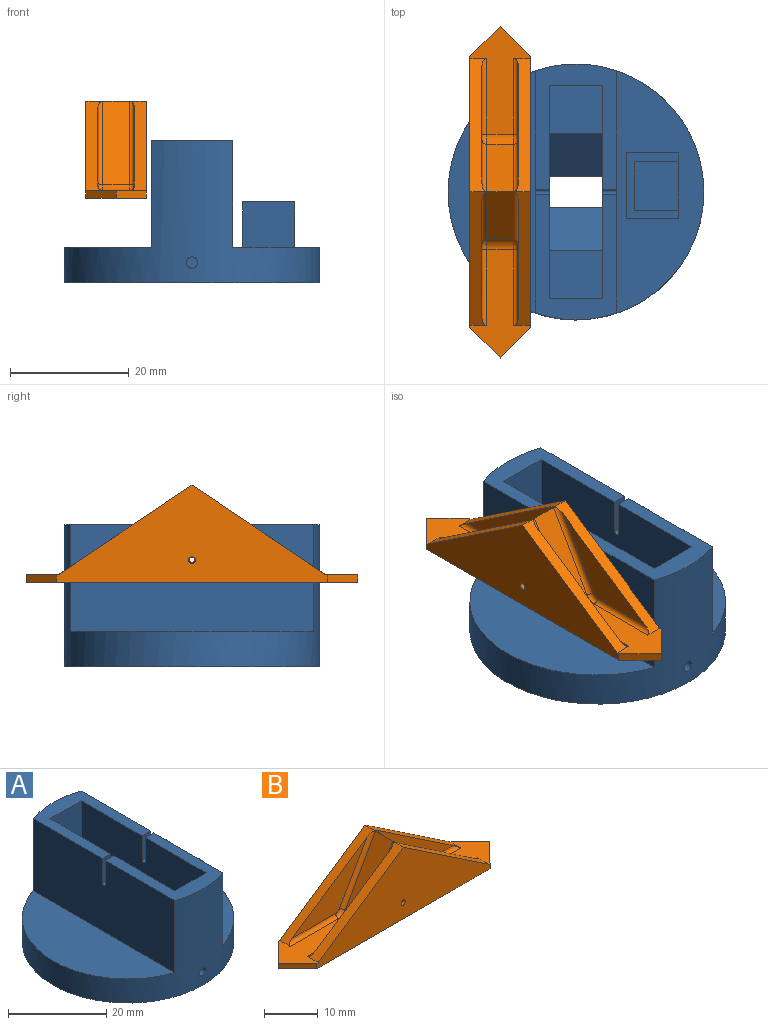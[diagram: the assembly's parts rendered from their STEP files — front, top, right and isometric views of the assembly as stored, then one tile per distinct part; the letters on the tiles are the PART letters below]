
ASSEMBLY  parts=2 mates=1
PART A: 39 faces, bbox 43.1x43.1x24 mm
  f0: cylinder r=21.57mm len=43.14mm, axis (0,0,-1), area 1313.1mm2, adj f3,f5,f6,f7,f9,f10,f14,f35
  f1: plane 7.48x0.75mm, normal (0,1,0), area 5.6mm2, adj f24,f27,f28,f32
  f2: plane 7.48x0.75mm, normal (0,-1,0), area 5.6mm2, adj f24,f27,f28,f32
  f3: plane 40.87x14.67mm, normal (0,0,1), area 340.8mm2, adj f0,f6,f24,f29,f31,f34
  f4: plane 9x8.08mm, normal (0,0,1), area 72.7mm2, adj f8,f12,f13,f21
  f5: plane 21.12x13.8mm, normal (0,0,1), area 128.3mm2, adj f0,f6,f7,f8,f11,f12,f16,f18
  f6: plane 40.87x18mm, normal (1,0,0), area 730mm2, adj f0,f3,f5,f14,f16,f17,f22
  f7: plane 40.87x18mm, normal (-1,0,0), area 730mm2, adj f0,f5,f9,f14,f18,f19,f23
  f8: plane 36x24mm, normal (1,0,0), area 717.5mm2, adj f4,f5,f10,f11,f13,f14,f15,f18
  f9: plane 40.87x14.67mm, normal (0,0,1), area 438.3mm2, adj f0,f7
  f10: plane 43.14x43.14mm, normal (0,0,-1), area 1414.7mm2, adj f0,f8,f12,f20,f21
  f11: plane 18x9mm, normal (0,-1,0), area 162mm2, adj f5,f8,f12,f15
  f12: plane 36x24mm, normal (-1,0,0), area 717.5mm2, adj f4,f5,f10,f11,f13,f14,f15,f16
  f13: plane 18x9mm, normal (0,1,0), area 162mm2, adj f4,f8,f12,f14
  f14: plane 21.12x13.8mm, normal (0,0,1), area 128.3mm2, adj f0,f6,f7,f8,f12,f13,f17,f19
  f15: plane 9x8.08mm, normal (0,0,1), area 72.7mm2, adj f8,f11,f12,f20
  f16: plane 6x2.4mm, normal (0,-1,0), area 14.4mm2, adj f5,f6,f12,f22
  f17: plane 6x2.4mm, normal (0,1,0), area 14.4mm2, adj f6,f12,f14,f22
  f18: plane 6x2.4mm, normal (0,-1,0), area 14.4mm2, adj f5,f7,f8,f23
  f19: plane 6x2.4mm, normal (0,1,0), area 14.4mm2, adj f7,f8,f14,f23
  f20: plane 9x7.32mm, normal (0,-0.63,0.77), area 85.2mm2, adj f8,f10,f12,f15
  f21: plane 9x7.32mm, normal (0,0.63,0.77), area 85.2mm2, adj f4,f8,f10,f12
  f22: cylinder r=0.45mm len=2.4mm, axis (-1,0,0), area 3.4mm2, adj f6,f12,f16,f17
  f23: cylinder r=0.45mm len=2.4mm, axis (-1,0,0), area 3.4mm2, adj f7,f8,f18,f19
  f24: plane 11.1x7.65mm, normal (1,0,0), area 70.1mm2, adj f1,f2,f3,f25,f26,f27,f28,f29
  f25: plane 9.6x8.04mm, normal (0,0,1), area 77.2mm2, adj f24,f26,f30,f33
  f26: plane 8.04x0.9mm, normal (0,1,0), area 7.2mm2, adj f24,f25,f27,f33
  f27: plane 9.6x8.04mm, normal (0,0,-1), area 15.5mm2, adj f1,f2,f24,f26,f30,f32,f33
  f28: plane 11.1x8.79mm, normal (0,0,1), area 35.8mm2, adj f1,f2,f24,f29,f31,f32,f34
  f29: plane 8.79x7.65mm, normal (0,-1,0), area 67.2mm2, adj f3,f24,f28,f34
  f30: plane 8.04x0.9mm, normal (0,-1,0), area 7.2mm2, adj f24,f25,f27,f33
  f31: plane 8.79x7.65mm, normal (0,1,0), area 67.2mm2, adj f3,f24,f28,f34
  f32: plane 8.25x0.75mm, normal (1,0,0), area 6.2mm2, adj f1,f2,f27,f28
  f33: plane 9.6x0.9mm, normal (1,0,0), area 8.6mm2, adj f25,f26,f27,f30
  f34: plane 11.1x7.65mm, normal (-1,0,0), area 84.9mm2, adj f3,f28,f29,f31
  f35: cylinder r=0.96mm len=7.5mm, axis (0,-1,0), area 45.2mm2, adj f0,f36
  f36: plane 1.92x1.92mm, normal (0,-1,0), area 2.9mm2, adj f35
  f37: cylinder r=0.96mm len=7.5mm, axis (0,1,0), area 45.2mm2, adj f0,f38
  f38: plane 1.92x1.92mm, normal (0,1,0), area 2.9mm2, adj f37
PART B: 34 faces, bbox 56x10.2x16.8 mm
  f0: plane 18.24x10.2mm, normal (0,0,1), area 87.7mm2, adj f3,f4,f8,f9,f13,f14,f19,f27
  f1: plane 19.82x13.32mm, normal (0,1,0), area 81.5mm2, adj f5,f24,f25,f26
  f2: plane 19.82x13.32mm, normal (0,-1,0), area 81.5mm2, adj f6,f21,f22,f23
  f3: plane 22.5x15.12mm, normal (0.56,0,0.83), area 55.9mm2, adj f0,f5,f8,f15,f30,f32
  f4: plane 22.5x15.12mm, normal (0.56,0,0.83), area 55.9mm2, adj f0,f6,f9,f16,f27,f29
  f5: plane 22.5x15.12mm, normal (-0.56,0,0.83), area 55.9mm2, adj f1,f3,f7,f8,f24,f26
  f6: plane 22.5x15.12mm, normal (-0.56,0,0.83), area 55.9mm2, adj f2,f4,f7,f9,f21,f23
  f7: plane 18.24x10.2mm, normal (0,0,1), area 87.7mm2, adj f5,f6,f8,f9,f11,f12,f20,f21
  f8: plane 45.84x16.4mm, normal (0,-1,0), area 397.9mm2, adj f0,f3,f5,f7,f10,f12,f14,f33
  f9: plane 45.83x16.4mm, normal (0,1,0), area 397.9mm2, adj f0,f4,f6,f7,f10,f11,f13,f33
  f10: plane 56x10.2mm, normal (0,0,-1), area 519.4mm2, adj f8,f9,f11,f12,f13,f14
  f11: plane 5.1x5.08mm, normal (-0.71,0.71,0), area 9.2mm2, adj f7,f9,f10,f12
  f12: plane 5.1x5.08mm, normal (-0.71,-0.71,0), area 9.2mm2, adj f7,f8,f10,f11
  f13: plane 5.1x5.08mm, normal (0.71,0.71,0), area 9.2mm2, adj f0,f9,f10,f14
  f14: plane 5.1x5.08mm, normal (0.71,-0.71,0), area 9.2mm2, adj f0,f8,f10,f13
  f15: plane 19.82x13.32mm, normal (0,1,0), area 81.5mm2, adj f3,f30,f31,f32
  f16: plane 19.82x13.32mm, normal (0,-1,0), area 81.5mm2, adj f4,f27,f28,f29
  f17: plane 14.11x8.03mm, normal (0.87,0,0.49), area 73.4mm2, adj f18,f19,f29,f32
  f18: plane 14.11x8.03mm, normal (-0.87,0,0.49), area 73.4mm2, adj f17,f20,f23,f26
  f19: cylinder r=2mm len=4.52mm, axis (0,1,0), area 9.5mm2, adj f0,f17,f28,f31
  f20: cylinder r=2mm len=4.52mm, axis (0,-1,0), area 9.5mm2, adj f7,f18,f22,f25
  f21: cylinder r=0.8mm len=12.74mm, axis (1,0,0), area 15.5mm2, adj f2,f6,f7,f22
  f22: torus R=1.2mm, axis (0,-1,0), area 2.3mm2, adj f2,f20,f21,f23
  f23: cylinder r=0.8mm len=14.5mm, axis (0.49,0,0.87), area 19.7mm2, adj f2,f6,f18,f22
  f24: cylinder r=0.8mm len=12.74mm, axis (-1,0,0), area 15.5mm2, adj f1,f5,f7,f25
  f25: torus R=1.2mm, axis (0,1,0), area 2.3mm2, adj f1,f20,f24,f26
  f26: cylinder r=0.8mm len=14.5mm, axis (-0.49,0,-0.87), area 19.7mm2, adj f1,f5,f18,f25
  f27: cylinder r=0.8mm len=12.74mm, axis (1,0,0), area 15.5mm2, adj f0,f4,f16,f28
  f28: torus R=1.2mm, axis (0,-1,0), area 2.3mm2, adj f16,f19,f27,f29
  f29: cylinder r=0.8mm len=14.5mm, axis (0.49,0,-0.87), area 19.7mm2, adj f4,f16,f17,f28
  f30: cylinder r=0.8mm len=12.74mm, axis (-1,0,0), area 15.5mm2, adj f0,f3,f15,f31
  f31: torus R=1.2mm, axis (0,1,0), area 2.3mm2, adj f15,f19,f30,f32
  f32: cylinder r=0.8mm len=14.5mm, axis (-0.49,0,0.87), area 19.7mm2, adj f3,f15,f17,f31
  f33: cylinder r=0.55mm len=10.2mm, axis (0,-1,0), area 35.2mm2, adj f8,f9
PLACE A t=(-76.12,-27.27,13.27)mm
PLACE B rot(axis=(0,0,1),90deg) t=(-88.92,-27.27,27.52)mm
MATE slider B.f33 <-> A.f22  axis (-1,0,0) through (-94.02,-27.27,31.27)mm
